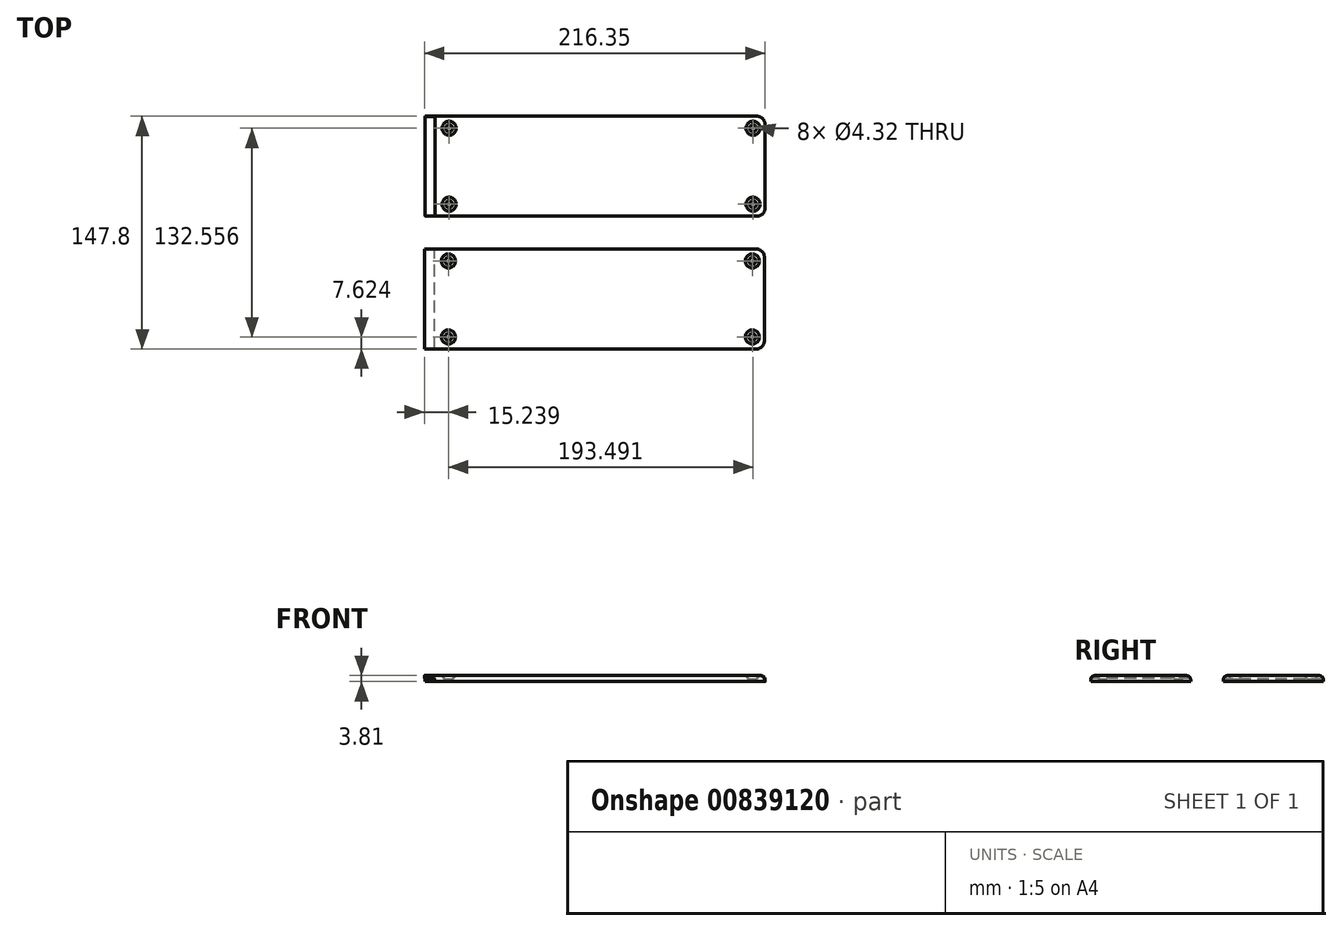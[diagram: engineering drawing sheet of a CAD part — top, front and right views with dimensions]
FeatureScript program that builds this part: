
annotation { "Feature Type Name" : "Feature", "Feature Type Description" : "" }
export const myFeature = defineFeature(function(context is Context, id is Id, definition is map)
    precondition{}
    {
        {
            var Q0;
            Q0=qCreatedBy(makeId("Top.planeOp"),FACE);
            var sketch = newSketch(context, id + "F0", { "sketchPlane" : qUnion([Q0])});
            skLineSegment(sketch, "E0.bottom", {"start": v(107.95, 31.75) * mm, "end": v(-107.95, 31.75) * mm});
            skLineSegment(sketch, "E0.top", {"start": v(107.95, -31.75) * mm, "end": v(-107.95, -31.75) * mm});
            skLineSegment(sketch, "E0.left", {"start": v(107.95, 31.75) * mm, "end": v(107.95, -31.75) * mm});
            skLineSegment(sketch, "E0.right", {"start": v(-107.95, 31.75) * mm, "end": v(-107.95, -31.75) * mm});
            skPoint(sketch, "E0.middle", {"position": v(0, 0) * mm});
            skCircle(sketch, "E1", {"center": v(-92.71, 24.13) * mm, "radius": 2.16 * mm});
            skCircle(sketch, "E2", {"center": v(-92.71, -24.13) * mm, "radius": 2.16 * mm});
            skCircle(sketch, "E3", {"center": v(100.33, 24.13) * mm, "radius": 2.16 * mm});
            skCircle(sketch, "E4", {"center": v(100.33, -24.13) * mm, "radius": 2.16 * mm});
            skSolve(sketch);
        }
        {
            var Q0;
            Q0=makeQuery(id+"F0.imprint","IMPRINT",FACE,{"disambiguationData":[TD([[makeQuery(id+"F0.imprint","IMPRINT",EDGE,{"derivedFrom":sQuery(id+"F0.wireOp",EDGE,"E0.bottom")}),1.0]])]});
            extrude(context, id + "F1", {"entities" : qUnion([Q0]), "depth" : 3.8 * mm, "offsetDistance" : 25.4 * mm});
        }
        {
            var Q0;
            Q0=makeQuery(id+"F1.opExtrude","CAP_FACE",FACE,{"disambiguationData":[OSD([sQuery(id+"F0.wireOp",EDGE,"E0.bottom"),sQuery(id+"F0.wireOp",EDGE,"E0.top"),sQuery(id+"F0.wireOp",EDGE,"E0.left"),sQuery(id+"F0.wireOp",EDGE,"E0.right"),sQuery(id+"F0.wireOp",EDGE,"E1"),sQuery(id+"F0.wireOp",EDGE,"E2"),sQuery(id+"F0.wireOp",EDGE,"E3"),sQuery(id+"F0.wireOp",EDGE,"E4")])],"isStart":false});
            var sketch = newSketch(context, id + "F2", { "sketchPlane" : qUnion([Q0])});
            skLineSegment(sketch, "E5.bottom", {"start": v(-107.95, 31.75) * mm, "end": v(-101.6, 31.75) * mm});
            skLineSegment(sketch, "E5.top", {"start": v(-107.95, -31.75) * mm, "end": v(-101.6, -31.75) * mm});
            skLineSegment(sketch, "E5.left", {"start": v(-107.95, 31.75) * mm, "end": v(-107.95, -31.75) * mm});
            skLineSegment(sketch, "E5.right", {"start": v(-101.6, 31.75) * mm, "end": v(-101.6, -31.75) * mm});
            skSolve(sketch);
        }
        {
            var Q0;
            Q0=makeQuery(id+"F2.imprint","IMPRINT",FACE,{"disambiguationData":[TD([[makeQuery(id+"F2.imprint","IMPRINT",EDGE,{"derivedFrom":sQuery(id+"F2.wireOp",EDGE,"E5.bottom")}),1.0]])]});
            extrude(context, id + "F3", {"entities" : qUnion([Q0]), "operationType" : NewBodyOperationType.REMOVE, "oppositeDirection" : true, "depth" : 2.03 * mm, "offsetDistance" : 25.4 * mm});
        }
        {
            var Q0;
            Q0=makeQuery(id+"F1.opExtrude","CAP_EDGE",EDGE,{"disambiguationData":[OSD([sQuery(id+"F0.wireOp",EDGE,"E1")])],"isStart":false});
            var Q1;
            Q1=makeQuery(id+"F1.opExtrude","CAP_EDGE",EDGE,{"disambiguationData":[OSD([sQuery(id+"F0.wireOp",EDGE,"E2")])],"isStart":false});
            var Q2;
            Q2=makeQuery(id+"F1.opExtrude","CAP_EDGE",EDGE,{"disambiguationData":[OSD([sQuery(id+"F0.wireOp",EDGE,"E3")])],"isStart":false});
            var Q3;
            Q3=makeQuery(id+"F1.opExtrude","CAP_EDGE",EDGE,{"disambiguationData":[OSD([sQuery(id+"F0.wireOp",EDGE,"E4")])],"isStart":false});
            chamfer(context, id + "F4", {"entities" : qUnion([Q0, Q1, Q2, Q3]), "width" : 2.3 * mm});
        }
        {
            var Q0;
            Q0=qCreatedBy(makeId("Top.planeOp"),FACE);
            var sketch = newSketch(context, id + "F5", { "sketchPlane" : qUnion([Q0])});
            skLineSegment(sketch, "E6.bottom", {"start": v(-108.4, -52.55) * mm, "end": v(107.5, -52.55) * mm});
            skLineSegment(sketch, "E6.top", {"start": v(-108.4, -116.05) * mm, "end": v(107.5, -116.05) * mm});
            skLineSegment(sketch, "E6.left", {"start": v(-108.4, -52.55) * mm, "end": v(-108.4, -116.05) * mm});
            skLineSegment(sketch, "E6.right", {"start": v(107.5, -52.55) * mm, "end": v(107.5, -116.05) * mm});
            skCircle(sketch, "E7", {"center": v(-93.16, -60.17) * mm, "radius": 2.16 * mm});
            skCircle(sketch, "E8", {"center": v(-93.16, -108.43) * mm, "radius": 2.16 * mm});
            skCircle(sketch, "E9", {"center": v(99.88, -108.43) * mm, "radius": 2.16 * mm});
            skCircle(sketch, "E10", {"center": v(99.88, -60.17) * mm, "radius": 2.16 * mm});
            skSolve(sketch);
        }
        {
            var Q0;
            Q0=makeQuery(id+"F5.imprint","IMPRINT",FACE,{"disambiguationData":[TD([[makeQuery(id+"F5.imprint","IMPRINT",EDGE,{"derivedFrom":sQuery(id+"F5.wireOp",EDGE,"E6.bottom")}),-1.0]])]});
            extrude(context, id + "F6", {"entities" : qUnion([Q0]), "depth" : 3.8 * mm, "offsetDistance" : 25.4 * mm});
        }
        {
            var Q0;
            Q0=makeQuery(id+"F6.opExtrude","CAP_EDGE",EDGE,{"disambiguationData":[OSD([sQuery(id+"F5.wireOp",EDGE,"E7")])],"isStart":false});
            var Q1;
            Q1=makeQuery(id+"F6.opExtrude","CAP_EDGE",EDGE,{"disambiguationData":[OSD([sQuery(id+"F5.wireOp",EDGE,"E10")])],"isStart":false});
            var Q2;
            Q2=makeQuery(id+"F6.opExtrude","CAP_EDGE",EDGE,{"disambiguationData":[OSD([sQuery(id+"F5.wireOp",EDGE,"E9")])],"isStart":false});
            var Q3;
            Q3=makeQuery(id+"F6.opExtrude","CAP_EDGE",EDGE,{"disambiguationData":[OSD([sQuery(id+"F5.wireOp",EDGE,"E8")])],"isStart":false});
            chamfer(context, id + "F7", {"entities" : qUnion([Q0, Q1, Q2, Q3]), "width" : 2.3 * mm, "tangentPropagation" : true});
        }
        {
            var Q0;
            Q0=makeQuery(id+"F6.opExtrude","CAP_FACE",FACE,{"disambiguationData":[OSD([sQuery(id+"F5.wireOp",EDGE,"E6.bottom"),sQuery(id+"F5.wireOp",EDGE,"E6.top"),sQuery(id+"F5.wireOp",EDGE,"E6.left"),sQuery(id+"F5.wireOp",EDGE,"E6.right"),sQuery(id+"F5.wireOp",EDGE,"E7"),sQuery(id+"F5.wireOp",EDGE,"E8"),sQuery(id+"F5.wireOp",EDGE,"E9"),sQuery(id+"F5.wireOp",EDGE,"E10")])],"isStart":true});
            var sketch = newSketch(context, id + "F8", { "sketchPlane" : qUnion([Q0])});
            skLineSegment(sketch, "E11.bottom", {"start": v(-108.4, 116.05) * mm, "end": v(-102.05, 116.05) * mm});
            skLineSegment(sketch, "E11.top", {"start": v(-108.4, 52.55) * mm, "end": v(-102.05, 52.55) * mm});
            skLineSegment(sketch, "E11.left", {"start": v(-108.4, 116.05) * mm, "end": v(-108.4, 52.55) * mm});
            skLineSegment(sketch, "E11.right", {"start": v(-102.05, 116.05) * mm, "end": v(-102.05, 52.55) * mm});
            skSolve(sketch);
        }
        {
            var Q0;
            Q0=makeQuery(id+"F8.imprint","IMPRINT",FACE,{"disambiguationData":[TD([[makeQuery(id+"F8.imprint","IMPRINT",EDGE,{"derivedFrom":sQuery(id+"F8.wireOp",EDGE,"E11.bottom")}),-1.0]])]});
            extrude(context, id + "F9", {"entities" : qUnion([Q0]), "operationType" : NewBodyOperationType.REMOVE, "oppositeDirection" : true, "depth" : 2.03 * mm, "offsetDistance" : 25.4 * mm});
        }
        {
            var Q0;
            Q0=makeQuery(id+"F1.opExtrude","SWEPT_EDGE",EDGE,{"disambiguationData":[OSD([sQuery(id+"F0.wireOp",EDGE,"E0.bottom"),sQuery(id+"F0.wireOp",EDGE,"E0.left")])]});
            var Q1;
            Q1=makeQuery(id+"F1.opExtrude","SWEPT_EDGE",EDGE,{"disambiguationData":[OSD([sQuery(id+"F0.wireOp",EDGE,"E0.top"),sQuery(id+"F0.wireOp",EDGE,"E0.left")])]});
            var Q2;
            Q2=makeQuery(id+"F6.opExtrude","SWEPT_EDGE",EDGE,{"disambiguationData":[OSD([sQuery(id+"F5.wireOp",EDGE,"E6.top"),sQuery(id+"F5.wireOp",EDGE,"E6.right")])]});
            var Q3;
            Q3=makeQuery(id+"F6.opExtrude","SWEPT_EDGE",EDGE,{"disambiguationData":[OSD([sQuery(id+"F5.wireOp",EDGE,"E6.bottom"),sQuery(id+"F5.wireOp",EDGE,"E6.right")])]});
            fillet(context, id + "F10", {"entities" : qUnion([Q0, Q1, Q2, Q3]), "radius" : 5.08 * mm, "tangentPropagation" : true, "allowEdgeOverflow" : false});
        }
        {
            var Q0;
            Q0=makeQuery(id+"F1.opExtrude","CAP_EDGE",EDGE,{"disambiguationData":[OSD([sQuery(id+"F0.wireOp",EDGE,"E0.bottom")])],"isStart":false});
            var Q1;
            Q1=makeQuery(id+"F6.opExtrude","CAP_EDGE",EDGE,{"disambiguationData":[OSD([sQuery(id+"F5.wireOp",EDGE,"E6.bottom")])],"isStart":false});
            fillet(context, id + "F11", {"entities" : qUnion([Q0, Q1]), "radius" : 2.54 * mm, "tangentPropagation" : true, "allowEdgeOverflow" : false});
        }
    });
